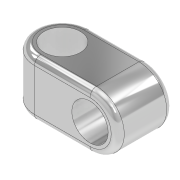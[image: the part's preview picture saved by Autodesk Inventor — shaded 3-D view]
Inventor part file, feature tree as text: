
AUTODESK INVENTOR PART (.ipt)
format: ipt  version: 2020 (Build 240168000, 168)  size: 158,208 bytes
history: native  units: mm
features: extrude x3, sketch x3, fillet x1
ambient origin geometry x8: Origin, YZ Plane, XZ Plane, XY Plane, X Axis, Y Axis, Z Axis, Center Point
bodies: Solid1 (feature_tree)
feature tree (7):
  extrude  "Extrusion1"  Depth=2.75mm
  extrude  "Extrusion2"  Depth=2.75mm
  extrude  "Extrusion3"  Depth=0.3248mm
  fillet  "Fillet1"  Radius=2.75mm
  sketch  "Sketch1"  dims[d0=5.5mm d1=2.75mm]
  sketch  "Sketch2"  dims[d2=2.75mm d3=0.0mm d4=1.8mm]
  sketch  "Sketch3"  dims[d5=0.0mm d6=0.0mm d7=1.8mm d8=2.75mm d9=0.0mm d10=0.3248mm]
